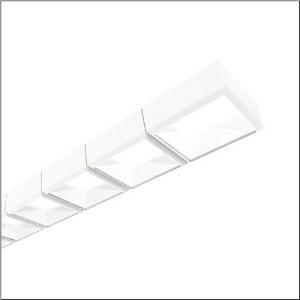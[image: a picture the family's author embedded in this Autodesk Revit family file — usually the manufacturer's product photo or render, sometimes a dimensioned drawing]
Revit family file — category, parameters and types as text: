
# Revit family: scriptus_r__11_5mz313d04wa_45ce
name_source: partatom
category: Lighting Fixtures
units: mm (PartAtom-declared; Revit-internal decimal feet)

## family parameters
Cut with Voids When Loaded = No
Host = Face
Light Source = No
Part Type = Normal
Room Calculation Point = No
Round Connector Dimension = Use Diameter
Shared = No

## types (1)
- Scriptus® 11 (1 x LED 4000K / CRI = 80 (unbekannt), 2660 lm / 4010 lm, 4000K)
    Apparent Load = 99 VA
    CIE Flux Codes = - - - 0 100 / 82 95 99 100 100
    Color Rendering = 80
    Color Temperature = 4000K
    Default Elevation = 1800 mm
    Description = Scriptus® 11, office luminaire, primary optical cover: lenses, CAT 2 (L<= 3000cd/m²), light emission: direct/indirect distribution, primary light characteristic: symmetric, installation type: suspended mounting, LED rated luminous flux: 13.330 lm, light colour: 840, colour temperature: 4000K, control gear: ECG DALI, with terminal, 5-pole, mains connection: 230V, AC, 50Hz, rated input power: 99W, LED control gear: ECG DALI, housing, luminaire housing, of aluminium, traffic white (RAL 9016), length: 2.648 mm, width: 114 mm, height: 57mm, protection rating (complete): IP20, insulation class (complete): insulation class I (protective earthing), certification: CE, ENEC, VDE, protection symbol: F, permissible ambient temperature for indoor applications: 0..+35°C, standard: EN 50419, packaging unit: 1 piece
    Height = 57 mm
    Lamp = 1 x LED 4000K / CRI >= 80 (unbekannt)
    Lamp Light Flux = 2660 lm / 4010 lm
    Lamp count = 1
    Length = 2648 mm
    Luminous efficacy = 134 lm/W
    Manufacturer = Siteco
    ModVariant = No
    Model = 5MZ313D04WA
    Mounting Place = Ceiling
    Mounting Type = Pendant
    Number of Poles = 1
    OnlyDefault = Yes
    Power Factor = 1
    Product Name = Scriptus® 11
    Product group = office luminaire | ceiling pendant
    ProductGroupID = 905
    Protection Class = Protection class I
    Protection Degree = IP 20
    RLX_Detail_Level = 1
    RlxData = <blob elided: 31617 chars, md5=e786bd34>
    Socket = socket
    Standby Power = 0 W
    System Light Flux = 13340 lm
    System Power = 99 W
    Type Comments = Product without accessories
    Type Image = l_1004839.jpg
    URL = http://relux.com
    VarID = ---
    Voltage = 0 V
    Weight = 0.00 kg
    Width = 114 mm

## geometry (parser evidence)
native form markers: Blend x4, Sweep x20
no freeform markers — native parametric forms only
